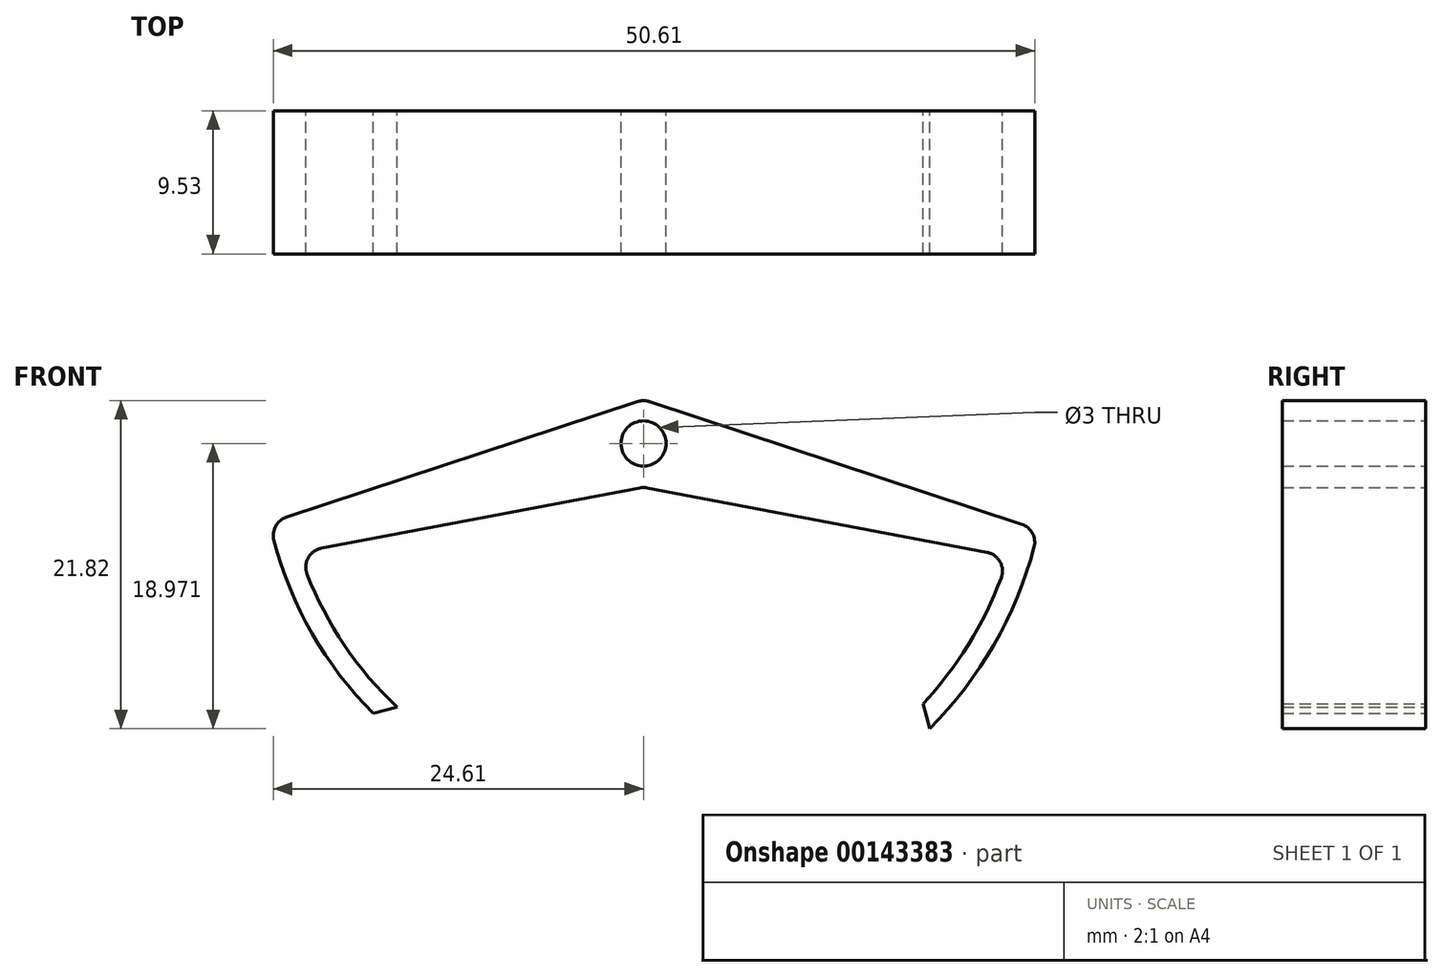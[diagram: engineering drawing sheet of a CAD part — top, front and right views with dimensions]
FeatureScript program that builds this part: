
annotation { "Feature Type Name" : "Feature", "Feature Type Description" : "" }
export const myFeature = defineFeature(function(context is Context, id is Id, definition is map)
    precondition{}
    {
        {
            var Q0;
            Q0=qCreatedBy(makeId("Front.planeOp"),FACE);
            var sketch = newSketch(context, id + "F0", { "sketchPlane" : qUnion([Q0])});
            skArc(sketch, "E0", {"start": v(-24.57, 14.8) * mm, "mid": v(-22.03, 8.6) * mm, "end": v(-17.96, 3.27) * mm});
            skLineSegment(sketch, "E1", {"start": v(-17.96, 3.27) * mm, "end": v(-16.37, 3.7) * mm});
            skLineSegment(sketch, "E2", {"start": v(18.58, 3.9) * mm, "end": v(19.02, 2.26) * mm});
            skArc(sketch, "E3", {"start": v(19.02, 2.26) * mm, "mid": v(23.28, 7.84) * mm, "end": v(25.96, 14.33) * mm});
            skLineSegment(sketch, "E4", {"start": v(-0.24, 18.28) * mm, "end": v(-21.42, 14.25) * mm});
            skLineSegment(sketch, "E5", {"start": v(-0.4, 24.01) * mm, "end": v(-23.74, 16.32) * mm});
            skLineSegment(sketch, "E6.MirrorCS", {"start": v(0.4, 24.01) * mm, "end": v(25.13, 15.86) * mm});
            skLineSegment(sketch, "E7.MirrorCS", {"start": v(0.24, 18.28) * mm, "end": v(22.82, 13.99) * mm});
            skPoint(sketch, "E8.orphan", {"position": v(-32.7, 12.11) * mm});
            skPoint(sketch, "E9.orphan", {"position": v(-40.06, 10.94) * mm});
            skPoint(sketch, "E10.orphan", {"position": v(32.7, 12.11) * mm});
            skPoint(sketch, "E11.orphan", {"position": v(40.06, 10.94) * mm});
            skArc(sketch, "E12.trimOffspring", {"start": v(-22.36, 12.55) * mm, "mid": v(-19.87, 7.78) * mm, "end": v(-16.37, 3.7) * mm});
            skArc(sketch, "E13.trimOffspring", {"start": v(18.58, 3.9) * mm, "mid": v(21.59, 7.85) * mm, "end": v(23.78, 12.3) * mm});
            skCircle(sketch, "E14", {"center": v(0, 21.23) * mm, "radius": 1.5 * mm});
            skPoint(sketch, "E15.visualSharp", {"position": v(-24.85, 15.95) * mm});
            skArc(sketch, "E15.filletArc", {"start": v(-23.74, 16.32) * mm, "mid": v(-24.46, 15.72) * mm, "end": v(-24.57, 14.8) * mm});
            skPoint(sketch, "E16.visualSharp", {"position": v(26.24, 15.5) * mm});
            skArc(sketch, "E16.filletArc", {"start": v(25.96, 14.33) * mm, "mid": v(25.85, 15.26) * mm, "end": v(25.13, 15.86) * mm});
            skPoint(sketch, "E17.visualSharp", {"position": v(24.26, 13.71) * mm});
            skArc(sketch, "E17.filletArc", {"start": v(23.78, 12.3) * mm, "mid": v(23.7, 13.36) * mm, "end": v(22.82, 13.99) * mm});
            skPoint(sketch, "E18.visualSharp", {"position": v(-22.87, 13.98) * mm});
            skArc(sketch, "E18.filletArc", {"start": v(-21.42, 14.25) * mm, "mid": v(-22.3, 13.62) * mm, "end": v(-22.36, 12.55) * mm});
            skPoint(sketch, "E19.visualSharp", {"position": v(0, 24.14) * mm});
            skArc(sketch, "E19.filletArc", {"start": v(0.4, 24.01) * mm, "mid": v(0, 24.08) * mm, "end": v(-0.4, 24.01) * mm});
            skPoint(sketch, "E20.visualSharp", {"position": v(0, 18.32) * mm});
            skArc(sketch, "E20.filletArc", {"start": v(0.24, 18.28) * mm, "mid": v(0, 18.3) * mm, "end": v(-0.24, 18.28) * mm});
            skSolve(sketch);
        }
        {
            var Q0;
            Q0=qSketchRegion(id+"F0",true);
            extrude(context, id + "F1", {"entities" : qUnion([Q0]), "depth" : 9.52 * mm});
        }
    });
